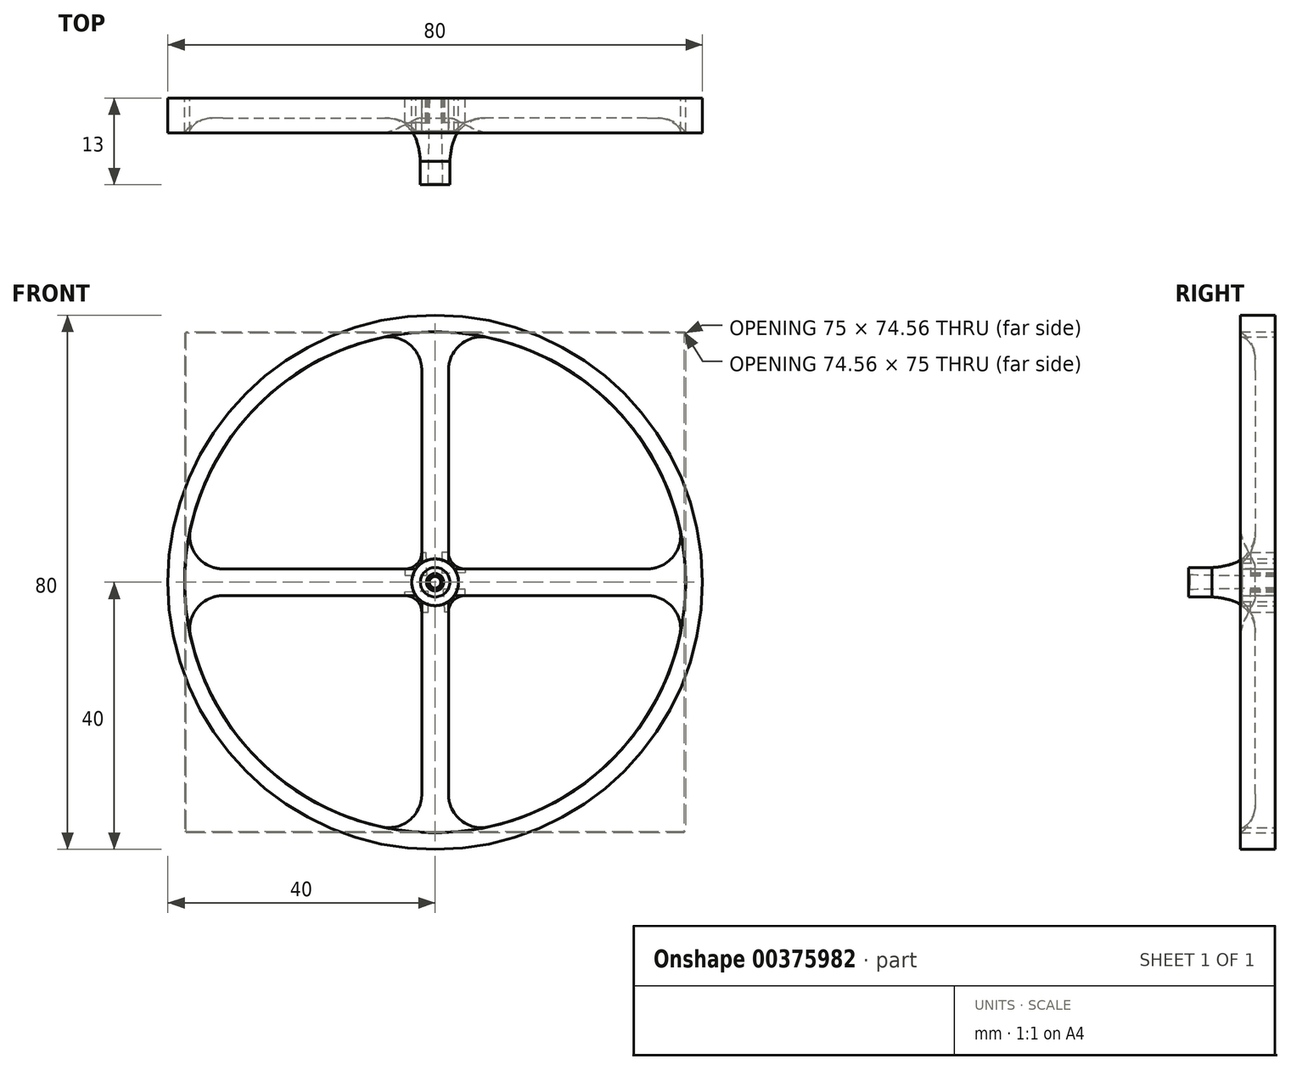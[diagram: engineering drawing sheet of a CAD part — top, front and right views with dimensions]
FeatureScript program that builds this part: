
annotation { "Feature Type Name" : "Feature", "Feature Type Description" : "" }
export const myFeature = defineFeature(function(context is Context, id is Id, definition is map)
    precondition{}
    {
        {
            var Q0;
            Q0=qCreatedBy(makeId("Front.planeOp"),FACE);
            var sketch = newSketch(context, id + "F0", { "sketchPlane" : qUnion([Q0])});
            skCircle(sketch, "E0", {"center": v(0, 0) * mm, "radius": 3.5 * mm});
            skSolve(sketch);
        }
        {
            var Q0;
            Q0=qSketchRegion(id+"F0",true);
            extrude(context, id + "F1", {"entities" : qUnion([Q0]), "depth" : 5 * mm});
        }
        {
            var Q0;
            Q0=qCreatedBy(makeId("Right.planeOp"),FACE);
            var sketch = newSketch(context, id + "F2", { "sketchPlane" : qUnion([Q0])});
            skLineSegment(sketch, "E1", {"start": v(3.77, 0) * mm, "end": v(-36.31, 0) * mm, "construction": true});
            skLineSegment(sketch, "E2", {"start": v(-13, 0) * mm, "end": v(-13, 2.2) * mm});
            skLineSegment(sketch, "E3", {"start": v(-13, 2.2) * mm, "end": v(-9.5, 2.2) * mm});
            skFitSpline(sketch, "E4", {"points": [v(-9.5, 2.2) * mm, v(-5, 3.5) * mm], "startDerivative": vector(5.34, 0.31) * mm, "endDerivative": vector(2.38, 2.14) * mm});
            skLineSegment(sketch, "E5", {"start": v(-5, 3.5) * mm, "end": v(-5, 0) * mm});
            skLineSegment(sketch, "E6", {"start": v(-5, 0) * mm, "end": v(-13, 0) * mm});
            skSolve(sketch);
        }
        {
            var Q0;
            Q0=qSketchRegion(id+"F2",true);
            var Q1;
            Q1=sQuery(id+"F2.wireOp",EDGE,"E1");
            revolve(context, id + "F3", {"operationType" : NewBodyOperationType.ADD, "entities" : qUnion([Q0]), "axis" : qUnion([Q1]), "revolveType" : RevolveType.FULL});
        }
        {
            var Q0;
            Q0=makeQuery(id+"F1.opExtrude","CAP_FACE",FACE,{"disambiguationData":[OSD([sQuery(id+"F0.wireOp",EDGE,"E0")])],"isStart":true});
            var sketch = newSketch(context, id + "F4", { "sketchPlane" : qUnion([Q0])});
            skCircle(sketch, "E7", {"center": v(0, 0) * mm, "radius": 0.85 * mm});
            skSolve(sketch);
        }
        {
            var Q0;
            Q0=qSketchRegion(id+"F4",true);
            extrude(context, id + "F5", {"entities" : qUnion([Q0]), "operationType" : NewBodyOperationType.REMOVE, "endBound" : BoundingType.THROUGH_ALL, "oppositeDirection" : true, "depth" : 25 * mm, "hasDraft" : true, "draftAngle" : 1.1 * degree});
        }
        {
            var Q0;
            Q0=qCreatedBy(makeId("Top.planeOp"),FACE);
            var sketch = newSketch(context, id + "F6", { "sketchPlane" : qUnion([Q0])});
            skLineSegment(sketch, "E8.bottom", {"start": v(-2, 0) * mm, "end": v(2, 0) * mm});
            skLineSegment(sketch, "E8.top", {"start": v(-2, -3) * mm, "end": v(2, -3) * mm});
            skLineSegment(sketch, "E8.left", {"start": v(-2, 0) * mm, "end": v(-2, -3) * mm});
            skLineSegment(sketch, "E8.right", {"start": v(2, 0) * mm, "end": v(2, -3) * mm});
            skSolve(sketch);
        }
        {
            var Q0;
            Q0=qSketchRegion(id+"F6",true);
            extrude(context, id + "F7", {"entities" : qUnion([Q0]), "operationType" : NewBodyOperationType.ADD, "depth" : 38 * mm, "hasSecondDirection" : true, "secondDirectionOppositeDirection" : false, "secondDirectionDepth" : 2.5 * mm});
        }
        {
            var Q0;
            Q0=makeQuery(id+"F5.boolean.opBoolean","INTERSECT",EDGE,{"derivedFrom":[makeQuery(id+"F3.opRevolve","SWEPT_FACE",FACE,{"disambiguationData":[OSD([sQuery(id+"F2.wireOp",EDGE,"E2")])]}),makeQuery(id+"F5.opExtrude","SWEPT_FACE",FACE,{"disambiguationData":[OSD([sQuery(id+"F4.wireOp",EDGE,"E7")])]})]});
            chamfer(context, id + "F8", {"entities" : qUnion([Q0]), "width" : .2 * mm, "tangentPropagation" : true});
        }
        {
            var Q0;
            Q0=makeQuery(id+"F7.boolean.opBoolean","MERGE",FACE,{"derivedFrom":[makeQuery(id+"F1.opExtrude","CAP_FACE",FACE,{"disambiguationData":[OSD([sQuery(id+"F0.wireOp",EDGE,"E0")])],"isStart":true}),makeQuery(id+"F7.opExtrude","SWEPT_FACE",FACE,{"disambiguationData":[OSD([sQuery(id+"F6.wireOp",EDGE,"E8.bottom")])]})]});
            var sketch = newSketch(context, id + "F9", { "sketchPlane" : qUnion([Q0])});
            skCircle(sketch, "E9", {"center": v(0, 0) * mm, "radius": 40 * mm});
            skCircle(sketch, "E10", {"center": v(0, 0) * mm, "radius": 37.5 * mm});
            skSolve(sketch);
        }
        {
            var Q0;
            Q0=qSketchRegion(id+"F9",true);
            extrude(context, id + "F10", {"entities" : qUnion([Q0]), "operationType" : NewBodyOperationType.ADD, "oppositeDirection" : true, "depth" : 5.2 * mm});
        }
        {
            var Q0;
            Q0=makeQuery(id+"F7.boolean.opBoolean","INTERSECT",EDGE,{"derivedFrom":[makeQuery(id+"F1.opExtrude","SWEPT_FACE",FACE,{"disambiguationData":[OSD([sQuery(id+"F0.wireOp",EDGE,"E0")])]}),makeQuery(id+"F7.opExtrude","SWEPT_FACE",FACE,{"disambiguationData":[OSD([sQuery(id+"F6.wireOp",EDGE,"E8.top")])]})]});
            var Q1;
            Q1=makeQuery(id+"F10.boolean.opBoolean","INTERSECT",EDGE,{"derivedFrom":[makeQuery(id+"F7.opExtrude","SWEPT_FACE",FACE,{"disambiguationData":[OSD([sQuery(id+"F6.wireOp",EDGE,"E8.top")])]}),makeQuery(id+"F10.opExtrude","SWEPT_FACE",FACE,{"disambiguationData":[OSD([sQuery(id+"F9.wireOp",EDGE,"E10")])]})]});
            fillet(context, id + "F11", {"entities" : qUnion([Q0, Q1]), "radius" : 5 * mm, "tangentPropagation" : true, "allowEdgeOverflow" : false});
        }
        {
            var Q0;
            Q0=makeQuery(id+"F10.boolean.opBoolean","INTERSECT",EDGE,{"derivedFrom":[makeQuery(id+"F7.opExtrude","SWEPT_FACE",FACE,{"disambiguationData":[OSD([sQuery(id+"F6.wireOp",EDGE,"E8.right")])]}),makeQuery(id+"F10.opExtrude","SWEPT_FACE",FACE,{"disambiguationData":[OSD([sQuery(id+"F9.wireOp",EDGE,"E10")])]})]});
            var Q1;
            Q1=makeQuery(id+"F10.boolean.opBoolean","INTERSECT",EDGE,{"derivedFrom":[makeQuery(id+"F7.opExtrude","SWEPT_FACE",FACE,{"disambiguationData":[OSD([sQuery(id+"F6.wireOp",EDGE,"E8.left")])]}),makeQuery(id+"F10.opExtrude","SWEPT_FACE",FACE,{"disambiguationData":[OSD([sQuery(id+"F9.wireOp",EDGE,"E10")])]})]});
            fillet(context, id + "F12", {"entities" : qUnion([Q0, Q1]), "radius" : 5 * mm, "tangentPropagation" : true, "allowEdgeOverflow" : false});
        }
        {
            var Q0;
            Q0=makeQuery(id+"F1.opExtrude","SWEPT_BODY",BODY,{"disambiguationData":[OSD([sQuery(id+"F0.wireOp",EDGE,"E0")])]});
            var Q1;
            Q1=makeQuery(id+"F3.opRevolve","SWEPT_FACE",FACE,{"disambiguationData":[OSD([sQuery(id+"F2.wireOp",EDGE,"E3")])]});
            circularPattern(context, id + "F13", {"entities" : qUnion([Q0]), "axis" : qUnion([Q1]), "angle" : 360 * degree, "instanceCount" : 4, "equalSpace" : true});
        }
        {
            var Q0;
            {var subQ0=makeQuery(id+"F10.boolean.opBoolean","MERGE",FACE,{"derivedFrom":[makeQuery(id+"F7.boolean.opBoolean","MERGE",FACE,{"derivedFrom":[makeQuery(id+"F1.opExtrude","CAP_FACE",FACE,{"disambiguationData":[OSD([sQuery(id+"F0.wireOp",EDGE,"E0")])],"isStart":true}),makeQuery(id+"F7.opExtrude","SWEPT_FACE",FACE,{"disambiguationData":[OSD([sQuery(id+"F6.wireOp",EDGE,"E8.bottom")])]})]}),makeQuery(id+"F10.opExtrude","CAP_FACE",FACE,{"disambiguationData":[OSD([sQuery(id+"F9.wireOp",EDGE,"E9"),sQuery(id+"F9.wireOp",EDGE,"E10")])],"isStart":true})]});Q0=makeQuery(id+"FgIhm2Tt6zTOsJ9_1.boolean.opBoolean","MERGE",FACE,{"derivedFrom":[makeQuery(id+"FDYBKFrb20v7z53_1.opBoolean","MERGE",FACE,{"derivedFrom":[subQ0,makeQuery(id+"F13.opPattern","COPY",FACE,{"derivedFrom":subQ0,"instanceName":"1"}),makeQuery(id+"F13.opPattern","COPY",FACE,{"derivedFrom":subQ0,"instanceName":"2"}),makeQuery(id+"F13.opPattern","COPY",FACE,{"derivedFrom":subQ0,"instanceName":"3"})]}),makeQuery(id+"FgIhm2Tt6zTOsJ9_1.opExtrude","CAP_FACE",FACE,{"disambiguationData":[OSD([sQuery(id+"FTYQuE2zEAQoyuF_1.wireOp",EDGE,"2QqTN2Jg-TwYb-xefx-Ns2m-0Et6M2J3xaq2"),sQuery(id+"FTYQuE2zEAQoyuF_1.wireOp",EDGE,"eRERD4EF-URZr-QwCf-6lY6-XNeSWXYZj7bk"),sQuery(id+"FTYQuE2zEAQoyuF_1.wireOp",EDGE,"w1udHuFG-gaxB-rpRy-TvAe-Q6hEAi3vOdkO"),sQuery(id+"FTYQuE2zEAQoyuF_1.wireOp",EDGE,"ccb8e607-9a5f-4511-8021-514936b70c73.filletArc"),sQuery(id+"FTYQuE2zEAQoyuF_1.wireOp",EDGE,"0a0adc1d-e557-4132-b897-d3ac198357fb.filletArc"),sQuery(id+"FTYQuE2zEAQoyuF_1.wireOp",EDGE,"b0aMqVTr-uXCx-4wKI-6uIc-G6YGe43DG1Aq"),sQuery(id+"FTYQuE2zEAQoyuF_1.wireOp",EDGE,"I1tABSEo-hI8d-lGJT-UJOT-oiTtTxIxys52"),sQuery(id+"FTYQuE2zEAQoyuF_1.wireOp",EDGE,"LAcF6vfi-sfcO-sjto-NgG3-pIlErQrigMXa"),sQuery(id+"FTYQuE2zEAQoyuF_1.wireOp",EDGE,"aqtcTmt6-T24C-q2HQ-cTpA-Y39zHsUlbNQ4")])],"isStart":true})]});}
            var sketch = newSketch(context, id + "F14", { "sketchPlane" : qUnion([Q0])});
            skArc(sketch, "E11", {"start": v(-4.5, 2) * mm, "mid": v(-2.73, 2.73) * mm, "end": v(-2, 4.5) * mm});
            skLineSegment(sketch, "E12", {"start": v(-2, 4.5) * mm, "end": v(-1.03, 4.5) * mm});
            skLineSegment(sketch, "E13", {"start": v(-1.03, 4.5) * mm, "end": v(-1.03, 1.28) * mm});
            skLineSegment(sketch, "E14", {"start": v(-4.5, 2) * mm, "end": v(-4.5, 1.43) * mm});
            skLineSegment(sketch, "E15", {"start": v(-4.5, 1.43) * mm, "end": v(-1.03, 1.28) * mm});
            skLineSegment(sketch, "E16.1.0", {"start": v(-4.5, -2) * mm, "end": v(-4.5, -1.03) * mm});
            skLineSegment(sketch, "E16.1.1", {"start": v(-4.5, -1.03) * mm, "end": v(-1.28, -1.03) * mm});
            skLineSegment(sketch, "E16.1.2", {"start": v(-1.43, -4.5) * mm, "end": v(-1.28, -1.03) * mm});
            skLineSegment(sketch, "E16.1.3", {"start": v(-2, -4.5) * mm, "end": v(-1.43, -4.5) * mm});
            skArc(sketch, "E16.1.4", {"start": v(-2, -4.5) * mm, "mid": v(-2.73, -2.73) * mm, "end": v(-4.5, -2) * mm});
            skLineSegment(sketch, "E16.2.0", {"start": v(2, -4.5) * mm, "end": v(1.03, -4.5) * mm});
            skLineSegment(sketch, "E16.2.1", {"start": v(1.03, -4.5) * mm, "end": v(1.03, -1.28) * mm});
            skLineSegment(sketch, "E16.2.2", {"start": v(4.5, -1.43) * mm, "end": v(1.03, -1.28) * mm});
            skLineSegment(sketch, "E16.2.3", {"start": v(4.5, -2) * mm, "end": v(4.5, -1.43) * mm});
            skArc(sketch, "E16.2.4", {"start": v(4.5, -2) * mm, "mid": v(2.73, -2.73) * mm, "end": v(2, -4.5) * mm});
            skLineSegment(sketch, "E16.3.0", {"start": v(4.5, 2) * mm, "end": v(4.5, 1.03) * mm});
            skLineSegment(sketch, "E16.3.1", {"start": v(4.5, 1.03) * mm, "end": v(1.28, 1.03) * mm});
            skLineSegment(sketch, "E16.3.2", {"start": v(1.43, 4.5) * mm, "end": v(1.28, 1.03) * mm});
            skLineSegment(sketch, "E16.3.3", {"start": v(2, 4.5) * mm, "end": v(1.43, 4.5) * mm});
            skArc(sketch, "E16.3.4", {"start": v(2, 4.5) * mm, "mid": v(2.73, 2.73) * mm, "end": v(4.5, 2) * mm});
            skPoint(sketch, "E16.center", {"position": v(0, 0) * mm});
            skSolve(sketch);
        }
        {
            var Q0;
            Q0=qSketchRegion(id+"F14",true);
            extrude(context, id + "F15", {"entities" : qUnion([Q0]), "oppositeDirection" : true, "depth" : 3.7 * mm});
        }
    });
